# Revit family: Modular_Desks-Teknion-RTLDC_Cross_Grain_Rectangular_Worksurface-R2019
name_source: partatom
category: Furniture
units: mm (PartAtom-declared; Revit-internal decimal feet)

## family parameters
Always vertical = Yes
Cut with Voids When Loaded = No
OmniClass Number = 23.40.20.00
OmniClass Title = General Furniture and Specialties
Room Calculation Point = No
Shared = Yes
Work Plane-Based = No

## types (6) — shared parameters
Assembly Code = E2020200
Manufacturer = Teknion
Manufacturer Fax = 416.661.4586
Part Number = RTLDC
Product Documentation Link = https://www.teknion.com
Product Documentation Link #2 = https://www.teknion.com
Product Documentation Link #3 = https://www.teknion.com
Product Documentation Link #4 = https://www.teknion.com
Product Documentation Link #5 = https://www.teknion.com
Product Documentation Link #6 = https://www.teknion.com
Product Documentation Link #7 = https://www.teknion.com
Product Documentation Link #8 = https://www.teknion.com
Product Documentation Link #9 = https://www.teknion.com
Product Line = Expansion Desking
Product Page URL = https://www.teknion.com
Series = Expansion Desking
Sustainability Data = https://www.teknion.com
URL = www.teknion.com
Unit Weight URL = http://www.teknion.com
Warranty = http://www.teknion.com

## per-type parameters (varying)
| type | Centered Grommet Option | Depth | Description | Model |
| 20" Depth, Centered Grommet | Yes | 20 " | Cross Grain Rectangular Worksurface, 20" Depth, Centered Grommet | RTLDC20__C |
| 24" Depth, Centered Grommet | Yes | 24 " | Cross Grain Rectangular Worksurface, 24" Depth, Centered Grommet | RTLDC24__C |
| 30" Depth, Centered Grommet | Yes | 30 " | Cross Grain Rectangular Worksurface, 30" Depth, Centered Grommet | RTLDC30__C |
| 20" Depth, No Grommet | No | 20 " | Cross Grain Rectangular Worksurface, 20" Depth, No Grommet | RTLDC20__N |
| 24" Depth, No Grommet | No | 24 " | Cross Grain Rectangular Worksurface, 24" Depth, No Grommet | RTLDC24__N |
| 30" Depth, No Grommet | No | 30 " | Cross Grain Rectangular Worksurface, 30" Depth, No Grommet | RTLDC30__N |

## geometry (parser evidence)
native form markers: Sweep x26
no freeform markers — native parametric forms only
